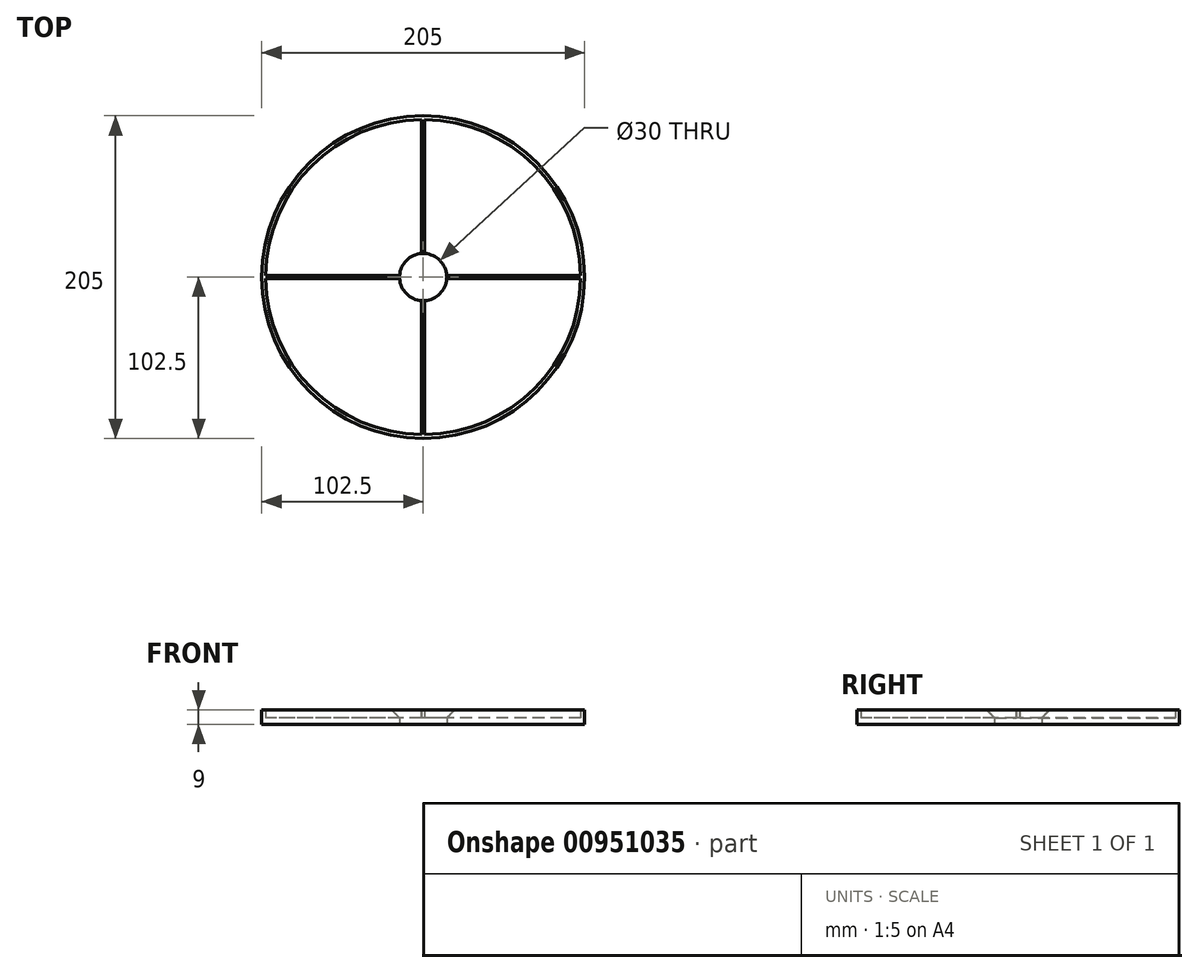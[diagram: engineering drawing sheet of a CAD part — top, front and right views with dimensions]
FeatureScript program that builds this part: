
annotation { "Feature Type Name" : "Feature", "Feature Type Description" : "" }
export const myFeature = defineFeature(function(context is Context, id is Id, definition is map)
    precondition{}
    {
        {
            var Q0;
            Q0=qCreatedBy(makeId("Top.planeOp"),FACE);
            var sketch = newSketch(context, id + "F0", { "sketchPlane" : qUnion([Q0])});
            skCircle(sketch, "E0", {"center": v(0, 0) * mm, "radius": 102.5 * mm});
            skCircle(sketch, "E1", {"center": v(0, 0) * mm, "radius": 15 * mm});
            skArc(sketch, "E2", {"start": v(100, 1) * mm, "mid": v(70.71, 70.71) * mm, "end": v(1, 100) * mm});
            skLineSegment(sketch, "E3.left", {"start": v(1, 100) * mm, "end": v(1, 14.97) * mm});
            skLineSegment(sketch, "E3.right", {"start": v(-1, 100) * mm, "end": v(-1, 14.97) * mm});
            skLineSegment(sketch, "E4.bottom", {"start": v(100, -1) * mm, "end": v(14.97, -1) * mm});
            skLineSegment(sketch, "E4.top", {"start": v(100, 1) * mm, "end": v(14.97, 1) * mm});
            skLineSegment(sketch, "E5.trimOffspring", {"start": v(1, -14.97) * mm, "end": v(1, -100) * mm});
            skLineSegment(sketch, "E6.trimOffspring", {"start": v(-1, -14.97) * mm, "end": v(-1, -100) * mm});
            skLineSegment(sketch, "E7.trimOffspring", {"start": v(-14.97, -1) * mm, "end": v(-100, -1) * mm});
            skLineSegment(sketch, "E8.trimOffspring", {"start": v(-14.97, 1) * mm, "end": v(-100, 1) * mm});
            skArc(sketch, "E9.trimOffspring", {"start": v(-1, 100) * mm, "mid": v(-70.71, 70.71) * mm, "end": v(-100, 1) * mm});
            skArc(sketch, "E10.trimOffspring", {"start": v(-100, -1) * mm, "mid": v(-70.71, -70.71) * mm, "end": v(-1, -100) * mm});
            skArc(sketch, "E11.trimOffspring", {"start": v(1, -100) * mm, "mid": v(70.71, -70.71) * mm, "end": v(100, -1) * mm});
            skSolve(sketch);
        }
        {
            var Q0;
            {var subQ0=sQuery(id+"F0.wireOp",EDGE,"E6.trimOffspring");Q0=makeQuery(id+"F0.imprint","IMPRINT",FACE,{"disambiguationData":[TD([[makeQuery(id+"F0.imprint","IMPRINT",EDGE,{"derivedFrom":subQ0}),-1.0]])]});}
            var Q1;
            {var subQ0=sQuery(id+"F0.wireOp",EDGE,"E4.bottom");Q1=makeQuery(id+"F0.imprint","IMPRINT",FACE,{"disambiguationData":[TD([[makeQuery(id+"F0.imprint","IMPRINT",EDGE,{"derivedFrom":subQ0}),1.0]])]});}
            var Q2;
            Q2=makeQuery(id+"F0.imprint","IMPRINT",FACE,{"disambiguationData":[TD([[makeQuery(id+"F0.imprint","IMPRINT",EDGE,{"derivedFrom":sQuery(id+"F0.wireOp",EDGE,"E2")}),1.0]])]});
            var Q3;
            {var subQ0=sQuery(id+"F0.wireOp",EDGE,"E3.right");Q3=makeQuery(id+"F0.imprint","IMPRINT",FACE,{"disambiguationData":[TD([[makeQuery(id+"F0.imprint","IMPRINT",EDGE,{"derivedFrom":subQ0}),-1.0]])]});}
            extrude(context, id + "F1", {"entities" : qUnion([Q0, Q1, Q2, Q3]), "depth" : 4 * mm, "offsetDistance" : 25 * mm});
        }
        {
            var Q0;
            Q0 = qSketchRegion(id + "F0", true);
            extrude(context, id + "F2", {"entities" : qUnion([Q0]), "operationType" : NewBodyOperationType.ADD, "depth" : 9 * mm, "offsetDistance" : 25 * mm});
        }
        {
            var Q0;
            {var subQ0=sQuery(id+"F0.wireOp",EDGE,"E1");Q0=makeQuery(id+"F2.opExtrude","CAP_EDGE",EDGE,{"disambiguationData":[OSD([subQ0]),TDD([makeQuery(id+"F0.imprint","IMPRINT",EDGE,{"disambiguationData":[TD([[makeQuery(id+"F0.imprint","INTERSECT",VERTEX,{"derivedFrom":[subQ0,sQuery(id+"F0.wireOp",EDGE,"E5.trimOffspring")]}),1.0]])],"derivedFrom":subQ0})])],"isStart":false});}
            var Q1;
            {var subQ0=sQuery(id+"F0.wireOp",EDGE,"E1");Q1=makeQuery(id+"F2.opExtrude","CAP_EDGE",EDGE,{"disambiguationData":[OSD([subQ0]),TDD([makeQuery(id+"F0.imprint","IMPRINT",EDGE,{"disambiguationData":[TD([[makeQuery(id+"F0.imprint","INTERSECT",VERTEX,{"derivedFrom":[subQ0,sQuery(id+"F0.wireOp",EDGE,"E7.trimOffspring")]}),1.0]])],"derivedFrom":subQ0})])],"isStart":false});}
            var Q2;
            {var subQ0=sQuery(id+"F0.wireOp",EDGE,"E1");Q2=makeQuery(id+"F2.opExtrude","CAP_EDGE",EDGE,{"disambiguationData":[OSD([subQ0]),TDD([makeQuery(id+"F0.imprint","IMPRINT",EDGE,{"disambiguationData":[TD([[makeQuery(id+"F0.imprint","INTERSECT",VERTEX,{"derivedFrom":[subQ0,sQuery(id+"F0.wireOp",EDGE,"E3.left")]}),-1.0]])],"derivedFrom":subQ0})])],"isStart":false});}
            var Q3;
            {var subQ0=sQuery(id+"F0.wireOp",EDGE,"E1");Q3=makeQuery(id+"F2.opExtrude","CAP_EDGE",EDGE,{"disambiguationData":[OSD([subQ0]),TDD([makeQuery(id+"F0.imprint","IMPRINT",EDGE,{"disambiguationData":[TD([[makeQuery(id+"F0.imprint","INTERSECT",VERTEX,{"derivedFrom":[subQ0,sQuery(id+"F0.wireOp",EDGE,"E4.bottom")]}),-1.0]])],"derivedFrom":subQ0})])],"isStart":false});}
            chamfer(context, id + "F3", {"entities" : qUnion([Q0, Q1, Q2, Q3]), "width" : 5 * mm, "tangentPropagation" : true});
        }
    });
